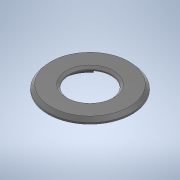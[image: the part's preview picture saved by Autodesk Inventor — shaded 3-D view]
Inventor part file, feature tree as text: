
AUTODESK INVENTOR PART (.ipt)
format: ipt  version: 2020 (Build 240168000, 168)  size: 272,896 bytes
history: native  units: mm
features: projected_geometry x6, sketch x5, revolve x3, chamfer x2, extrude x2, other x1, pattern_circular x1
ambient origin geometry x8: Origin, YZ Plane, XZ Plane, XY Plane, X Axis, Y Axis, Z Axis, Center Point
bodies: Body1 (feature_tree)
feature tree (20):
  other  "Твердое тело1"
  revolve  "Вращение1"
  chamfer  "Фаска1"  Distance=19.0mm
  chamfer  "Фаска2"  Distance=27.3mm
  revolve  "Вращение2"
  pattern_circular  "Круговой массив1"  [2 undecoded]
  extrude  "Выдавливание1"  TaperAngle=90.0deg  [1 undecoded]
  extrude  "Выдавливание2"  Depth=2.0mm TaperAngle=45.0deg
  revolve  "Вращение3"
  sketch  "Эскиз1"
  sketch  "Эскиз2"
  sketch  "Эскиз3"
  projected_geometry  "Спроецированная петля1"
  projected_geometry  "Спроецированная петля2"
  projected_geometry  "Спроецированная петля3"
  sketch  "Эскиз4"
  projected_geometry  "Спроецированная петля4"
  sketch  "Эскиз5"
  projected_geometry  "Спроецированная петля5"
  projected_geometry  "Спроецированная петля6"
note: 3 required parameter values undecoded (feature->parameter linkage not recoverable at this tier; creation-order binding heuristic only, values carry confidence <= 0.55)
